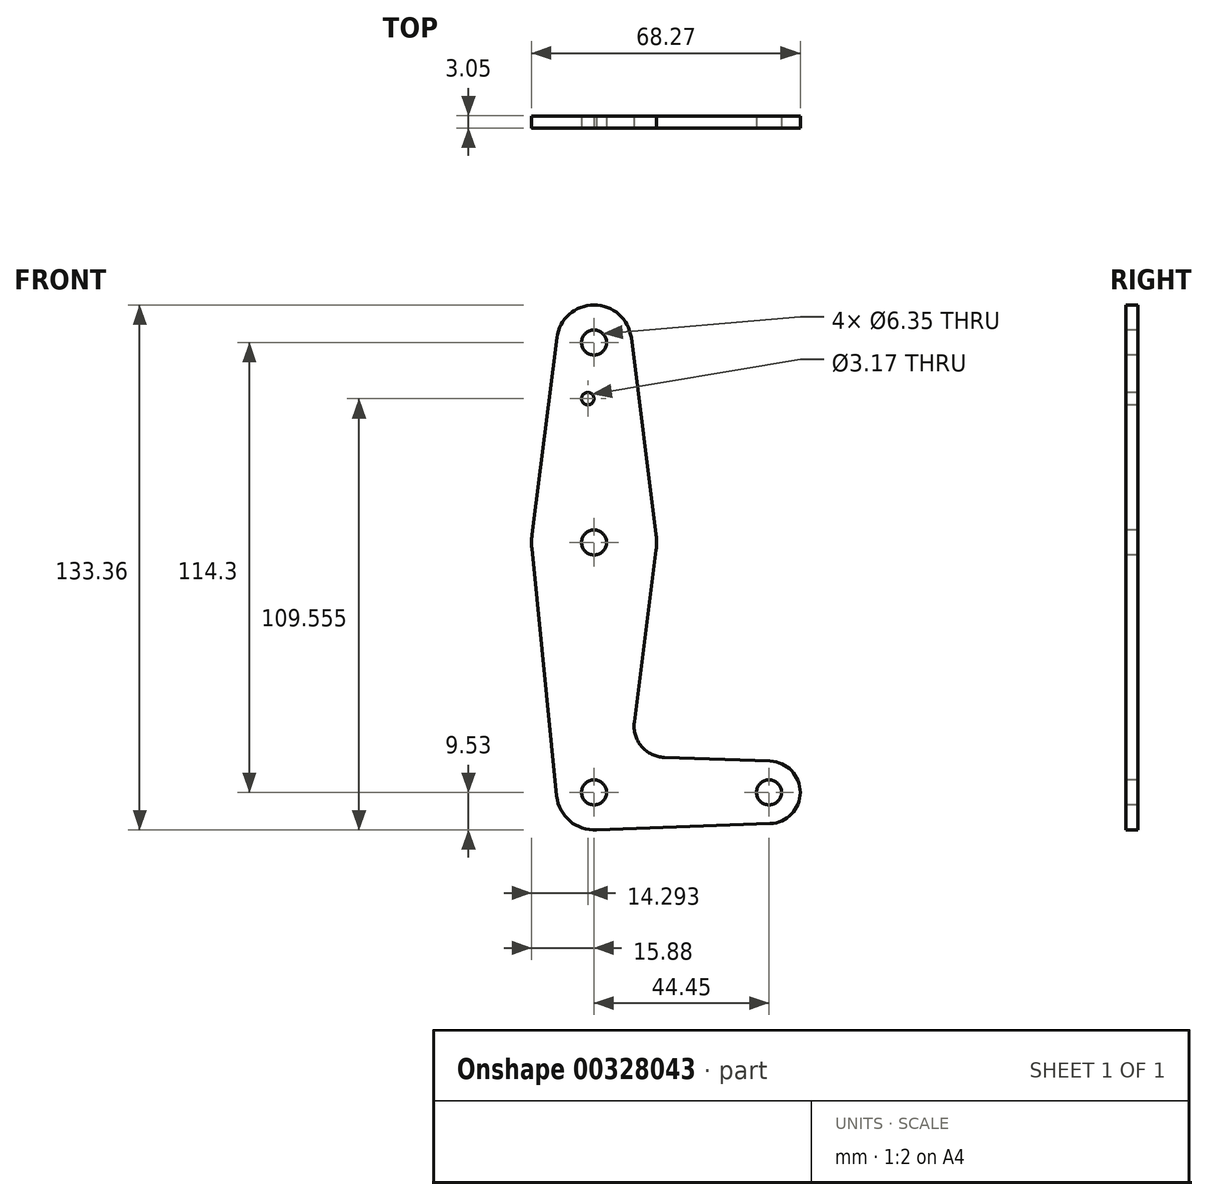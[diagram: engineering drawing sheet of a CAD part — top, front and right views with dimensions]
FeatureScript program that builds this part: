
annotation { "Feature Type Name" : "Feature", "Feature Type Description" : "" }
export const myFeature = defineFeature(function(context is Context, id is Id, definition is map)
    precondition{}
    {
        {
            var Q0;
            Q0=qCreatedBy(makeId("Front.planeOp"),FACE);
            var sketch = newSketch(context, id + "F0", { "sketchPlane" : qUnion([Q0])});
            skLineSegment(sketch, "E0", {"start": v(0, 114.3) * mm, "end": v(0, 0) * mm, "construction": true});
            skLineSegment(sketch, "E1", {"start": v(0, 0) * mm, "end": v(44.45, 0) * mm, "construction": true});
            skCircle(sketch, "E2", {"center": v(44.45, 0) * mm, "radius": 7.94 * mm});
            skCircle(sketch, "E3", {"center": v(0, 0) * mm, "radius": 9.53 * mm});
            skCircle(sketch, "E4", {"center": v(0, 114.3) * mm, "radius": 9.53 * mm});
            skCircle(sketch, "E5", {"center": v(0, 63.5) * mm, "radius": 15.88 * mm});
            skLineSegment(sketch, "E6", {"start": v(-9.45, 115.5) * mm, "end": v(-15.75, 65.48) * mm});
            skLineSegment(sketch, "E7", {"start": v(9.45, 115.5) * mm, "end": v(15.75, 65.48) * mm});
            skLineSegment(sketch, "E8", {"start": v(0, -9.53) * mm, "end": v(44.73, -7.93) * mm});
            skCircle(sketch, "E9", {"center": v(0, 114.3) * mm, "radius": 3.18 * mm});
            skCircle(sketch, "E10", {"center": v(-1.59, 100.03) * mm, "radius": 1.59 * mm});
            skCircle(sketch, "E11", {"center": v(0, 63.5) * mm, "radius": 3.18 * mm});
            skCircle(sketch, "E12", {"center": v(0, 0) * mm, "radius": 3.18 * mm});
            skCircle(sketch, "E13", {"center": v(44.45, 0) * mm, "radius": 3.18 * mm});
            skLineSegment(sketch, "E14", {"start": v(-15.8, 61.91) * mm, "end": v(-9.48, -0.95) * mm});
            skLineSegment(sketch, "E15", {"start": v(17.85, 8.9) * mm, "end": v(44.73, 7.93) * mm});
            skLineSegment(sketch, "E16", {"start": v(15.75, 61.52) * mm, "end": v(10.25, 17.83) * mm});
            skArc(sketch, "E17.filletArc", {"start": v(10.25, 17.83) * mm, "mid": v(12.08, 11.69) * mm, "end": v(17.85, 8.9) * mm});
            skSolve(sketch);
        }
        {
            var Q0;
            Q0 = qSketchRegion(id + "F0", true);
            extrude(context, id + "F1", {"entities" : qUnion([Q0]), "oppositeDirection" : true, "depth" : 3.05 * mm});
        }
    });
